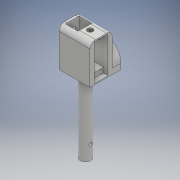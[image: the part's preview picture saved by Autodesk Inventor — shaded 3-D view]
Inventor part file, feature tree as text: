
AUTODESK INVENTOR PART (.ipt)
format: ipt  version: 2018 (Build 220112000, 112)  size: 382,976 bytes
history: native  units: mm
features: sketch x14, extrude x13, other x10, fillet x3
ambient origin geometry x8: Origin, YZ Plane, XZ Plane, XY Plane, X Axis, Y Axis, Z Axis, Center Point
bodies: Solid1 (feature_tree)
feature tree (40):
  extrude  "base"  Depth=20.0mm
  extrude  "attacher"  Depth=10.0mm
  fillet  "Fillet2"  Radius=9.5mm
  extrude  "hole_bar_rigify"  Depth=4.0mm
  extrude  "servo_place"  Depth=12.0mm TaperAngle=0.0deg
  extrude  "servo_place_2"  Depth=11.6mm
  fillet  "Fillet3"  Radius=12.5mm
  extrude  "rot_axis"  Depth=23.0mm TaperAngle=0.0deg
  extrude  "cable_hole"  Depth=4.7mm
  fillet  "Fillet5"  Radius=6.6mm
  extrude  "cable_guide_1"  Depth=5.0mm
  sketch  "Sketch23"  dims[d94=11.0mm d95=10.0mm]
  sketch  "Sketch24"  dims[d96=8.0mm d97=0.0mm d105=6.0mm]
  extrude  "cable_guide_2"  Depth=10.0mm
  extrude  "cable_guide_3"  Depth=6.0mm
  other  "cable_guide_4"
  extrude  "Extrusion25"  Depth=6.0mm
  other  "Edición directa1"
  other  "Edición directa2"
  other  "Edición directa3"
  other  "Edición directa4"
  extrude  "Extrusión26"  Depth=5.0mm
  extrude  "Extrusión27"  Depth=5.0mm
  sketch  "Sketch1"  dims[d0=25.0mm d1=20.0mm]
  sketch  "Sketch4"  dims[d2=35.0mm d3=0.0mm d18=10.0mm d19=9.5mm]
  sketch  "Sketch5"  dims[d20=100.0mm d21=0.0mm d22=4.0mm]
  sketch  "Sketch15"  dims[d23=5.0mm d24=12.0mm d25=0.0mm]
  sketch  "Sketch16"  dims[d76=6.25mm d77=11.6mm d78=12.5mm]
  sketch  "Sketch18"  dims[d79=23.2mm d80=23.0mm d81=0.0mm]
  sketch  "Sketch21"  dims[d82=4.7mm d83=4.7mm d84=6.6mm d85=0.0mm]
  sketch  "Sketch22"  dims[d92=20.0mm d93=5.0mm]
  sketch  "Sketch25"  dims[d106=10.0mm d107=0.0mm d108=6.0mm]
  sketch  "Sketch26"  dims[d109=10.0mm d110=5.0mm]
  sketch  "Boceto27"  dims[d111=5.0mm d112=5.0mm]
  sketch  "Boceto28"  dims[d113=5.0mm d114=15.0mm d115=15.0mm d116=5.0mm d117=15.0mm d118=8.0mm d119=0.0mm d120=2.0mm d121=11.0mm d122=7.0mm d123=2.0mm d124=11.0mm d125=7.0mm d126=8.0mm d127=0.0mm d128=8.0mm d129=0.0mm d130=90.0deg d131=13.0mm d132=3.0mm d133=10.0mm d134=0.0mm d135=0.0mm d136=0.0mm d137=-33.0mm d138=0.0mm d139=0.0mm d140=5.6mm d141=0.0mm d142=0.0mm d143=-2.6mm d144=-4.1mm d145=0.0mm d146=0.0mm d147=0.0mm d148=0.0mm d149=4.0mm d150=2.5mm d151=2.5mm d152=2.5mm d153=10.0mm d154=0.0mm d157=10.0mm d158=0.0mm]
  other  "Desplazar1"
  other  "Desplazar2"
  other  "Desplazar3"
  other  "Desplazar4"
  other  "Desplazar5"
